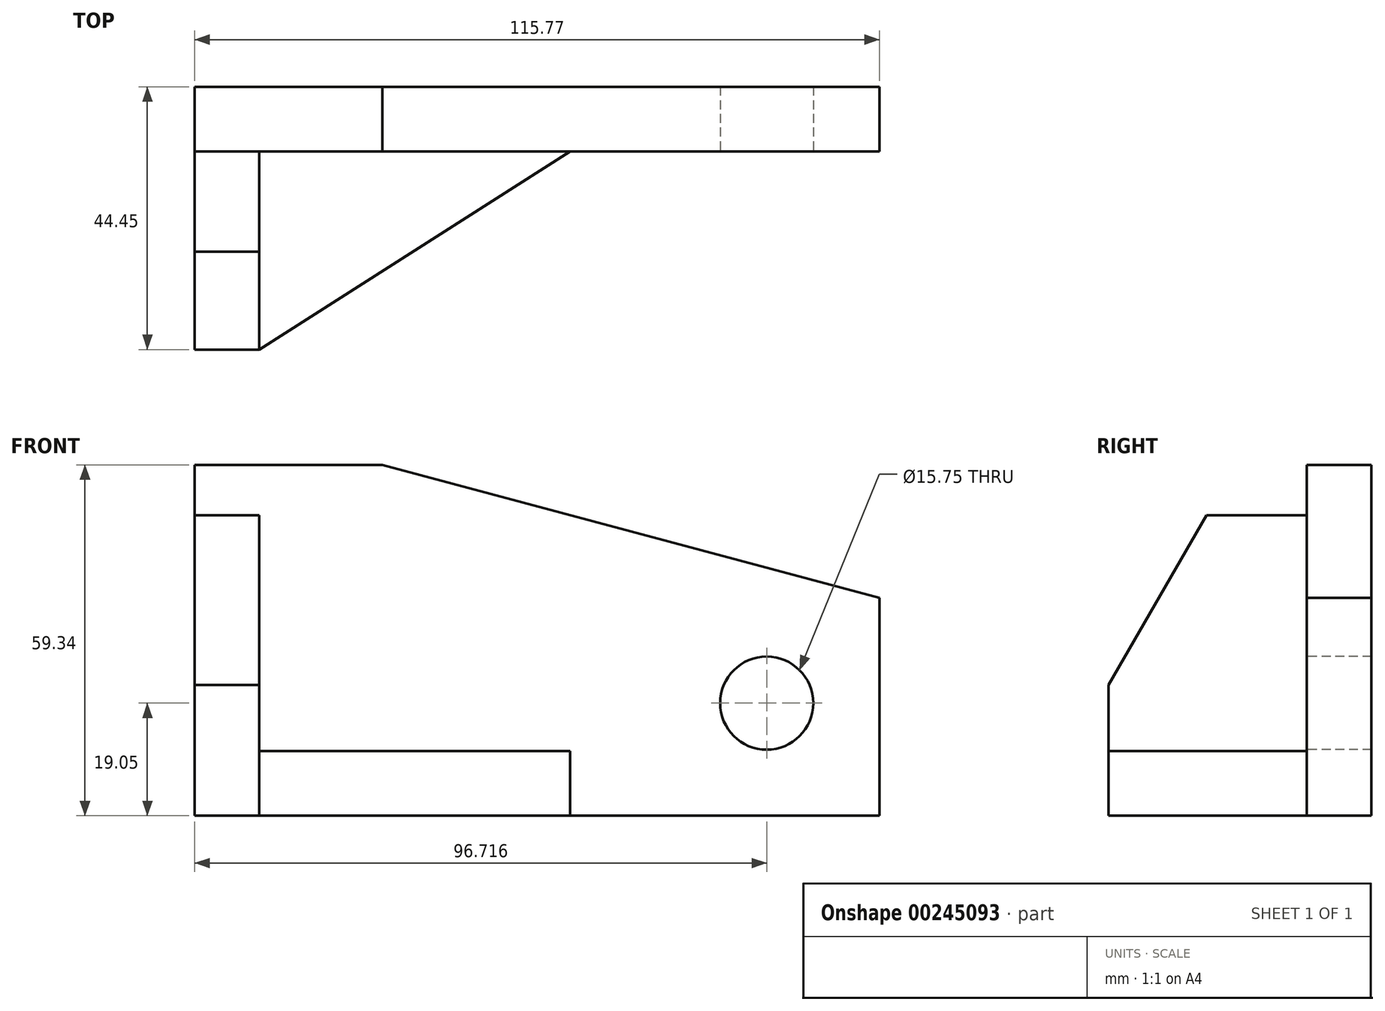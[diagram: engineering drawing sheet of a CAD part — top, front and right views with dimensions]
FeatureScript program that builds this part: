
annotation { "Feature Type Name" : "Feature", "Feature Type Description" : "" }
export const myFeature = defineFeature(function(context is Context, id is Id, definition is map)
    precondition{}
    {
        {
            var Q0;
            Q0=qCreatedBy(makeId("Front.planeOp"),FACE);
            var sketch = newSketch(context, id + "F0", { "sketchPlane" : qUnion([Q0])});
            skLineSegment(sketch, "E0.bottom", {"start": v(-46.18, 31.88) * mm, "end": v(-14.43, 31.88) * mm});
            skLineSegment(sketch, "E0.top", {"start": v(-46.18, -27.46) * mm, "end": v(-34.95, -27.46) * mm});
            skPoint(sketch, "E1", {"position": v(-14.43, 31.88) * mm});
            skLineSegment(sketch, "E2", {"start": v(-14.43, 31.88) * mm, "end": v(69.59, 31.88) * mm, "construction": true});
            skLineSegment(sketch, "E3", {"start": v(-14.43, 31.88) * mm, "end": v(69.59, 9.37) * mm});
            skPoint(sketch, "E4.orphan", {"position": v(-19.58, -48.13) * mm});
            skPoint(sketch, "E5.right.end.orphan", {"position": v(-27.42, -37.8) * mm});
            skPoint(sketch, "E6.center.orphan", {"position": v(49.07, -8.86) * mm});
            skLineSegment(sketch, "E7", {"start": v(69.59, -27.46) * mm, "end": v(69.59, 9.37) * mm});
            skPoint(sketch, "E8.bottom.end.orphan", {"position": v(-35.26, -27.46) * mm});
            skLineSegment(sketch, "E9", {"start": v(-34.95, -27.46) * mm, "end": v(69.59, -27.46) * mm});
            skPoint(sketch, "E10", {"position": v(17.32, -27.46) * mm});
            skPoint(sketch, "E11", {"position": v(-46.18, -5.36) * mm});
            skPoint(sketch, "E12.orphan", {"position": v(-46.18, 16.74) * mm});
            skLineSegment(sketch, "E13", {"start": v(-46.18, 31.88) * mm, "end": v(-46.18, -27.46) * mm});
            skSolve(sketch);
        }
        {
            var Q0;
            Q0=makeQuery(id+"F0.imprint","IMPRINT",FACE,{"disambiguationData":[TD([[makeQuery(id+"F0.imprint","IMPRINT",EDGE,{"derivedFrom":sQuery(id+"F0.wireOp",EDGE,"E0.bottom")}),-1.0]])]});
            extrude(context, id + "F1", {"entities" : qUnion([Q0]), "oppositeDirection" : true, "depth" : 10.92 * mm});
        }
        {
            var Q0;
            Q0=makeQuery(id+"F1.opExtrude","CAP_FACE",FACE,{"disambiguationData":[OSD([sQuery(id+"F0.wireOp",EDGE,"E0.bottom"),sQuery(id+"F0.wireOp",EDGE,"E0.top"),sQuery(id+"F0.wireOp",EDGE,"E3"),sQuery(id+"F0.wireOp",EDGE,"E7"),sQuery(id+"F0.wireOp",EDGE,"E9"),sQuery(id+"F0.wireOp",EDGE,"E13")])],"isStart":true});
            var sketch = newSketch(context, id + "F2", { "sketchPlane" : qUnion([Q0])});
            skLineSegment(sketch, "E14", {"start": v(-46.18, 23.34) * mm, "end": v(-35.26, 23.34) * mm});
            skLineSegment(sketch, "E15", {"start": v(-35.26, 23.34) * mm, "end": v(-35.26, -27.46) * mm});
            skLineSegment(sketch, "E16", {"start": v(-35.26, -16.54) * mm, "end": v(17.32, -16.54) * mm});
            skLineSegment(sketch, "E17", {"start": v(17.32, -16.54) * mm, "end": v(17.32, -27.46) * mm});
            skPoint(sketch, "E18.start.orphan", {"position": v(-46.18, -5.36) * mm});
            skSolve(sketch);
        }
        {
            var Q0;
            Q0 = qSketchRegion(id + "F2", true);
            var Q1;
            {var subQ3=sQuery(id+"F2.wireOp",EDGE,"E16");Q1=makeQuery(id+"F2.imprint","IMPRINT",FACE,{"disambiguationData":[TD([[makeQuery(id+"F2.imprint","IMPRINT",EDGE,{"derivedFrom":subQ3}),-1.0]])]});}
            var Q2;
            {var subQ0=sQuery(id+"F2.wireOp",EDGE,"E18");Q2=makeQuery(id+"F2.imprint","IMPRINT",FACE,{"disambiguationData":[TD([[makeQuery(id+"F2.imprint","IMPRINT",EDGE,{"derivedFrom":subQ0}),-1.0]])]});}
            var Q3;
            {var subQ0=sQuery(id+"F2.wireOp",EDGE,"E14");Q3=makeQuery(id+"F2.imprint","IMPRINT",FACE,{"disambiguationData":[TD([[makeQuery(id+"F2.imprint","IMPRINT",EDGE,{"derivedFrom":subQ0}),-1.0]])]});}
            extrude(context, id + "F3", {"entities" : qUnion([Q0, Q1, Q2, Q3]), "operationType" : NewBodyOperationType.ADD, "depth" : 33.53 * mm});
        }
        {
            var Q0;
            Q0=makeQuery(id+"F3.opExtrude","SWEPT_FACE",FACE,{"disambiguationData":[OSD([sQuery(id+"F2.wireOp",EDGE,"E16")])]});
            var sketch = newSketch(context, id + "F4", { "sketchPlane" : qUnion([Q0])});
            skLineSegment(sketch, "E19", {"start": v(17.32, 0) * mm, "end": v(-35.26, -33.53) * mm});
            skSolve(sketch);
        }
        {
            var Q0;
            Q0 = qSketchRegion(id + "F4", true);
            var Q1;
            Q1=makeQuery(id+"F4.imprint","IMPRINT",FACE,{"disambiguationData":[TD([[makeQuery(id+"F4.imprint","IMPRINT",EDGE,{"derivedFrom":sQuery(id+"F4.wireOp",EDGE,"E19")}),1.0]])]});
            extrude(context, id + "F5", {"entities" : qUnion([Q0, Q1]), "operationType" : NewBodyOperationType.REMOVE, "endBound" : BoundingType.THROUGH_ALL, "oppositeDirection" : true, "depth" : 25.4 * mm});
        }
        {
            var Q0;
            {var subQ0=sQuery(id+"F0.wireOp",EDGE,"E13");Q0=makeQuery(id+"F3.boolean.opBoolean","MERGE",FACE,{"derivedFrom":[makeQuery(id+"F1.opExtrude","SWEPT_FACE",FACE,{"disambiguationData":[OSD([subQ0])]}),makeQuery(id+"F3.opExtrude","SWEPT_FACE",FACE,{"disambiguationData":[OSD([subQ0])]})]});}
            var sketch = newSketch(context, id + "F6", { "sketchPlane" : qUnion([Q0])});
            skPoint(sketch, "E20", {"position": v(33.53, -5.36) * mm});
            skLineSegment(sketch, "E21", {"start": v(33.53, -5.36) * mm, "end": v(16.96, 23.34) * mm});
            skSolve(sketch);
        }
        {
            var Q0;
            Q0 = qSketchRegion(id + "F6", true);
            var Q1;
            {var subQ0=sQuery(id+"F6.wireOp",EDGE,"E21");Q1=makeQuery(id+"F6.imprint","IMPRINT",FACE,{"disambiguationData":[TD([[makeQuery(id+"F6.imprint","IMPRINT",EDGE,{"derivedFrom":subQ0}),-1.0]])]});}
            extrude(context, id + "F7", {"entities" : qUnion([Q0, Q1]), "operationType" : NewBodyOperationType.REMOVE, "endBound" : BoundingType.THROUGH_ALL, "oppositeDirection" : true, "depth" : 25.4 * mm});
        }
        {
            var Q0;
            Q0=makeQuery(id+"F1.opExtrude","CAP_FACE",FACE,{"disambiguationData":[OSD([sQuery(id+"F0.wireOp",EDGE,"E0.bottom"),sQuery(id+"F0.wireOp",EDGE,"E0.top"),sQuery(id+"F0.wireOp",EDGE,"E3"),sQuery(id+"F0.wireOp",EDGE,"E7"),sQuery(id+"F0.wireOp",EDGE,"E9"),sQuery(id+"F0.wireOp",EDGE,"E13")])],"isStart":true});
            var sketch = newSketch(context, id + "F8", { "sketchPlane" : qUnion([Q0])});
            skCircle(sketch, "E22", {"center": v(50.54, -8.4) * mm, "radius": 7.87 * mm});
            skSolve(sketch);
        }
        {
            var Q0;
            Q0=makeQuery(id+"F8.imprint","IMPRINT",FACE,{"disambiguationData":[TD([[makeQuery(id+"F8.imprint","IMPRINT",EDGE,{"derivedFrom":sQuery(id+"F8.wireOp",EDGE,"E22")}),1.0]])]});
            extrude(context, id + "F9", {"entities" : qUnion([Q0]), "operationType" : NewBodyOperationType.REMOVE, "endBound" : BoundingType.THROUGH_ALL, "oppositeDirection" : true, "depth" : 25.4 * mm});
        }
    });
